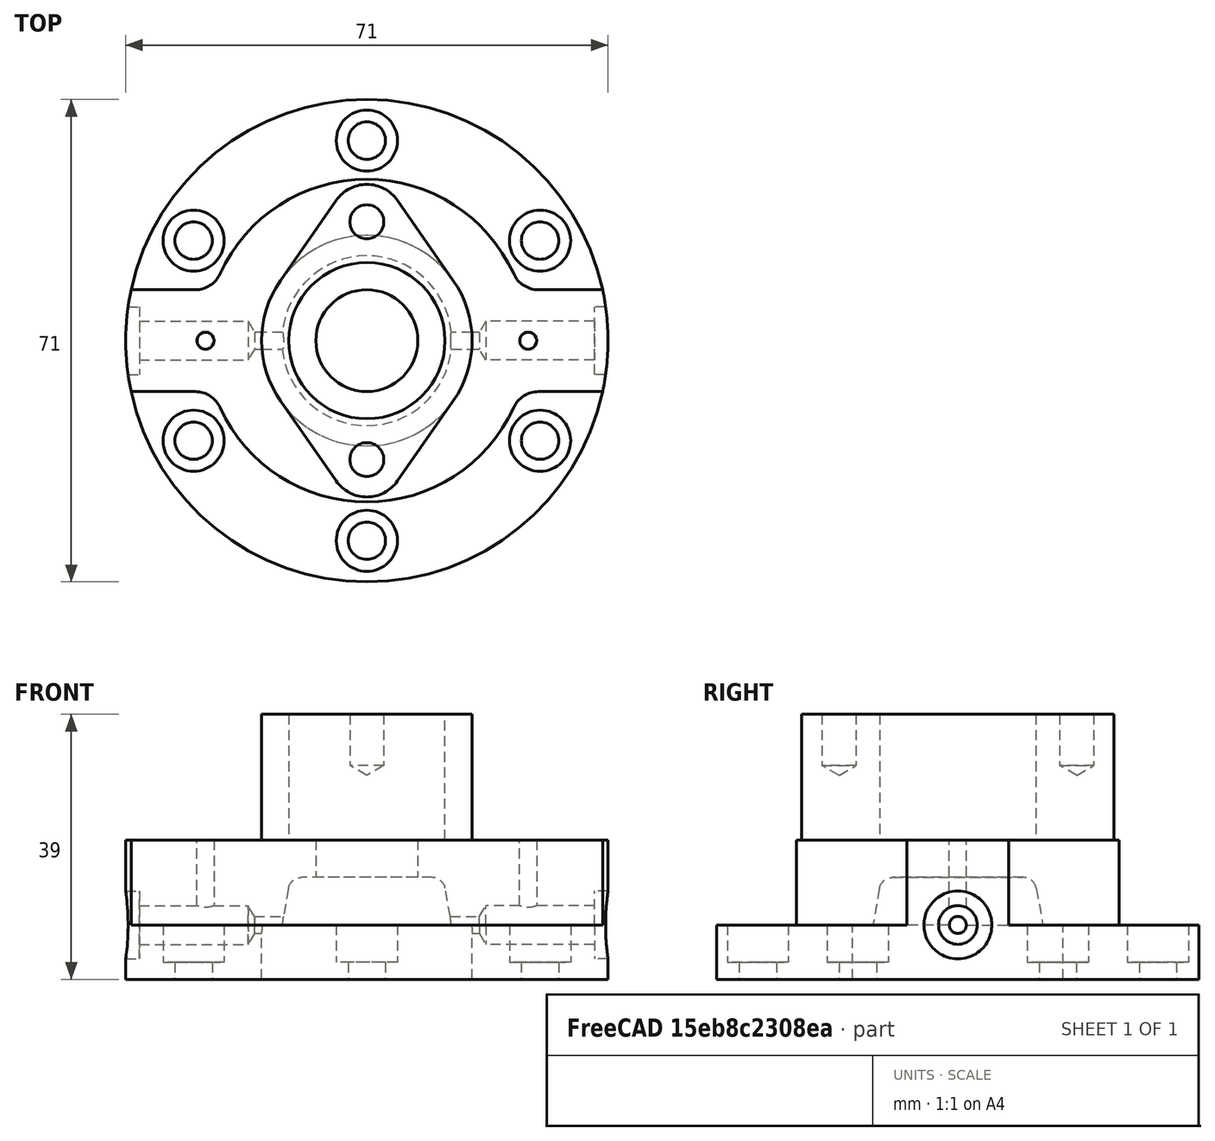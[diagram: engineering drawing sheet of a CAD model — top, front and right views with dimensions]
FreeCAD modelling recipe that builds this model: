
FCSTD DOCUMENT  (FreeCAD 1.1R40265 (Git))
Label: 0000
License: All rights reserved
LicenseURL: http://en.wikipedia.org/wiki/All_rights_reserved
objects: TechDraw::DrawViewDimension×33, Sketcher::SketchObject×10, PartDesign::Fillet×4, PartDesign::Pocket×3, PartDesign::Hole×3, TechDraw::DrawProjGroupItem×3, PartDesign::Mirrored×2, TechDraw::DrawViewSection×2, App::Point×1, PartDesign::Revolution×1, PartDesign::Pad×1, PartDesign::PolarPattern×1, Spreadsheet::Sheet×1, TechDraw::DrawSVGTemplate×1, PartDesign::Body×1, TechDraw::DrawViewAnnotation×1, TechDraw::DrawPage×1
note: 120 computed .brp shape members not serialized (recipe doc carries the construction recipe); baked Part::Feature solids carry a one-line shape summary decoded from their .brp

FEATURE [App::Point] Origin001
  Role = Origin
FEATURE [Sketcher::SketchObject] Sketch
  ArcFitTolerance = 1e-06
  AttachmentSupport = -> [XZ_Plane]
  ExternalTypes = [0]
  FullyConstrained = true
  MakeInternals = false
  MapMode = 5
  Placement = pos=(0,0,0) rot=(1,0,0;1.5708rad)
  expr: Constraints[0] = ModelParameters.Constraint_0_Distance
  expr: Constraints[12] = ModelParameters.Constraint_12_Distance
  expr: Constraints[15] = ModelParameters.Constraint_15_Distance
  expr: Constraints[18] = ModelParameters.Constraint_18_Distance
  expr: Constraints[22] = ModelParameters.Constraint_22_Angle
  expr: Constraints[25] = ModelParameters.Constraint_25_Radius
  expr: Constraints[3] = ModelParameters.Constraint_3_Distance
  expr: Constraints[6] = ModelParameters.Constraint_6_Distance
  expr: Constraints[9] = ModelParameters.Constraint_9_Distance
  sketch-geometry (10):
    g0: LineSegment [constr] StartX=0 StartY=0 StartZ=0 EndX=15.5 EndY=0 EndZ=0
    g1: LineSegment StartX=15.5 StartY=0 StartZ=0 EndX=35.5 EndY=0 EndZ=0
    g2: LineSegment StartX=35.5 StartY=0 StartZ=0 EndX=35.5 EndY=20.5 EndZ=0
    g3: LineSegment StartX=35.5 StartY=20.5 StartZ=0 EndX=7.5 EndY=20.5 EndZ=0
    g4: LineSegment StartX=7.5 StartY=20.5 StartZ=0 EndX=7.5 EndY=15 EndZ=0
    g5: LineSegment StartX=15.5 StartY=0 StartZ=0 EndX=15.5 EndY=8 EndZ=0
    g6: LineSegment StartX=15.5 StartY=8 StartZ=0 EndX=12.5 EndY=8 EndZ=0
    g7: LineSegment StartX=12.5 StartY=8 StartZ=0 EndX=11.5571 EndY=13.3473 EndZ=0
    g8: LineSegment StartX=7.5 StartY=15 StartZ=0 EndX=9.58751 EndY=15 EndZ=0
    g9: ArcOfCircle CenterX=9.58751 CenterY=13 CenterZ=0 NormalX=0 NormalY=0 NormalZ=1 AngleXU=0 Radius=2 StartAngle=0.174533 EndAngle=1.5708
  constraints (28):
    c: Distance(g0) = 15.5
    c: Coincident(g0,g-1)
    c: PointOnObject(g0,g-1)
    c: Distance(g1) = 20
    c: Coincident(g1,g0)
    c: PointOnObject(g1,g-1)
    c: Distance(g2) = 20.5
    c: Coincident(g2,g1)
    c: Vertical(g2)
    c: Distance(g3) = 28
    c: Coincident(g3,g2)
    c: Horizontal(g3)
    c: Distance(g4) = 5.5
    c: Coincident(g4,g3)
    c: Vertical(g4)
    c: Distance(g5) = 8
    c: Coincident(g5,g0)
    c: Vertical(g5)
    c: Distance(g6) = 3
    c: Coincident(g6,g5)
    c: Horizontal(g6)
    c: Coincident(g7,g6)
    c: Angle(g-2,g7) = 0.174533
    c: Coincident(g8,g4)
    c: Horizontal(g8)
    c: Radius(g9) = 2
    c: Tangent(g9,g7) = -1.5708
    c: Tangent(g9,g8) = 1.5708
FEATURE [PartDesign::Revolution] Revolution
  Angle = 360
  Angle2 = 60
  Axis = (0,2e-16,1)
  Base = (0,0,0)
  Placement = pos=(0,0,0) rot=(1,0,0;1.5708rad)
  Profile = -> Sketch
  ReferenceAxis = -> Sketch [V_Axis]
  Reversed = true
  Suppressed = false
  Type = 0
  expr: Angle = ModelParameters.Angle
FEATURE [Sketcher::SketchObject] Sketch001
  ArcFitTolerance = 1e-06
  AttachmentOffset = pos=(0,0,20.5) rot=(0,0,1;0rad)
  AttachmentSupport = -> [XY_Plane]
  ExternalTypes = [0]
  FullyConstrained = true
  MakeInternals = false
  MapMode = 5
  Placement = pos=(0,0,20.5) rot=(0,0,1;0rad)
  expr: Constraints[10] = ModelParameters.Constraint_9_Distance_001
  expr: Constraints[11] = ModelParameters.Constraint_9_Distance_001
  expr: Constraints[15] = ModelParameters.Constraint_15_Diameter_001
  expr: Constraints[19] = ModelParameters.Constraint_15_Diameter_001 / 2
  expr: Constraints[1] = ModelParameters.Constraint_1_Diameter
  expr: Constraints[22] = ModelParameters.Constraint_15_Diameter_001 / 2
  expr: Constraints[25] = ModelParameters.Constraint_25_Diameter
  expr: Constraints[27] = ModelParameters.Constraint_25_Diameter
  expr: Constraints[29] = ModelParameters.Constraint_29_Diameter
  expr: Constraints[38] = ModelParameters.Constraint_38_Distance
  expr: Constraints[8] = ModelParameters.Constraint_9_Distance_001
  expr: Constraints[9] = ModelParameters.Constraint_9_Distance_001
  sketch-geometry (14):
    g0: ArcOfCircle CenterX=0 CenterY=0 CenterZ=0 NormalX=0 NormalY=0 NormalZ=1 AngleXU=0 Radius=23.75 StartAngle=0.321289 EndAngle=2.8203
    g1: Circle [constr] CenterX=0 CenterY=0 CenterZ=0 NormalX=0 NormalY=0 NormalZ=1 AngleXU=0 Radius=35.5
    g2: LineSegment StartX=22.5347 StartY=-7.5 StartZ=0 EndX=34.6987 EndY=-7.5 EndZ=0
    g3: LineSegment StartX=-22.5347 StartY=7.5 StartZ=0 EndX=-34.6987 EndY=7.5 EndZ=0
    g4: LineSegment StartX=-22.5347 StartY=-7.5 StartZ=0 EndX=-34.6987 EndY=-7.5 EndZ=0
    g5: LineSegment StartX=22.5347 StartY=7.5 StartZ=0 EndX=34.6987 EndY=7.5 EndZ=0
    g6: ArcOfCircle CenterX=0 CenterY=0 CenterZ=0 NormalX=0 NormalY=0 NormalZ=1 AngleXU=0 Radius=23.75 StartAngle=3.46288 EndAngle=5.9619
    g7: LineSegment [constr] StartX=0 StartY=0 StartZ=0 EndX=23.75 EndY=0 EndZ=0
    g8: LineSegment [constr] StartX=0 StartY=0 StartZ=0 EndX=-23.75 EndY=0 EndZ=0
    g9: Circle CenterX=-23.75 CenterY=0 CenterZ=0 NormalX=0 NormalY=0 NormalZ=1 AngleXU=0 Radius=1.25
    g10: Circle CenterX=23.75 CenterY=0 CenterZ=0 NormalX=0 NormalY=0 NormalZ=1 AngleXU=0 Radius=1.25
    g11: Circle CenterX=0 CenterY=0 CenterZ=0 NormalX=0 NormalY=0 NormalZ=1 AngleXU=0 Radius=7.5
    g12: ArcOfCircle CenterX=0 CenterY=0 CenterZ=0 NormalX=0 NormalY=0 NormalZ=1 AngleXU=0 Radius=35.5 StartAngle=0.212872 EndAngle=2.92872
    g13: ArcOfCircle CenterX=-1.16293e-06 CenterY=0 CenterZ=0 NormalX=0 NormalY=0 NormalZ=1 AngleXU=0 Radius=35.5 StartAngle=3.35446 EndAngle=6.07031
  constraints (40):
    c: Coincident(g0,g-1)
    c: Diameter(g1) = 71
    c: Coincident(g1,g0)
    c: Horizontal(g2)
    c: PointOnObject(g3,g1)
    c: Horizontal(g3)
    c: Horizontal(g4)
    c: Horizontal(g5)
    c: Distance(g-1,g3) = 7.5
    c: Distance(g-1,g4) = 7.5
    c: Distance(g-1,g5) = 7.5
    c: Distance(g-1,g2) = 7.5
    c: Coincident(g2,g6)
    c: Coincident(g5,g0)
    c: Equal(g0,g6)
    c: Diameter(g0) = 47.5
    c: Coincident(g3,g0)
    c: Coincident(g4,g6)
    c: Coincident(g0,g6)
    c: Distance(g7) = 23.75
    c: Coincident(g7,g0)
    c: PointOnObject(g7,g-1)
    c: Distance(g8) = 23.75
    c: Coincident(g8,g0)
    c: PointOnObject(g8,g-1)
    c: Diameter(g9) = 2.5
    c: Coincident(g9,g8)
    c: Diameter(g10) = 2.5
    c: Coincident(g10,g7)
    c: Diameter(g11) = 15
    c: Coincident(g11,g0)
    c: Coincident(g12,g0)
    c: Coincident(g12,g3)
    c: Coincident(g12,g5)
    c: Coincident(g2,g13)
    c: Coincident(g4,g13)
    c: Block(g4)
    c: Block(g2)
    c: Distance(g4,g4) = 12.164
    c: Block(g13)
FEATURE [PartDesign::Pocket] Pocket
  BaseFeature = -> Revolution
  Direction = (0,0,-1)
  Length = 12.5
  Length2 = 5
  Placement = pos=(0,0,0) rot=(1,0,0;1.5708rad)
  Profile = -> Sketch001
  ReferenceAxis = -> Sketch001 [N_Axis]
  Suppressed = false
  Type = 0
  expr: Length = ModelParameters.Pocket_Length
  expr: TaperAngle = ModelParameters.Pocket_Taper_angle
FEATURE [Sketcher::SketchObject] Sketch002
  ArcFitTolerance = 1e-06
  AttachmentOffset = pos=(0,0,20.5) rot=(0,0,1;0rad)
  AttachmentSupport = -> [XY_Plane]
  ExternalTypes = [0]
  FullyConstrained = true
  MakeInternals = false
  MapMode = 5
  Placement = pos=(0,0,20.5) rot=(0,0,1;0rad)
  expr: Constraints[0] = ModelParameters.Constraint_0_Diameter
  expr: Constraints[22] = ModelParameters.Constraint_22_Radius
  expr: Constraints[4] = ModelParameters.Constraint_4_DistanceY
  expr: Constraints[5] = ModelParameters.Constraint_5_Radius
  sketch-geometry (12):
    g0: Circle CenterX=0 CenterY=0 CenterZ=0 NormalX=0 NormalY=0 NormalZ=1 AngleXU=0 Radius=11.5
    g1: Circle [constr] CenterX=0 CenterY=0 CenterZ=0 NormalX=0 NormalY=0 NormalZ=1 AngleXU=0 Radius=15.5
    g2: Circle [constr] CenterX=0 CenterY=17.5 CenterZ=0 NormalX=0 NormalY=0 NormalZ=1 AngleXU=0 Radius=5.5
    g3: Circle [constr] CenterX=0 CenterY=-17.5 CenterZ=0 NormalX=0 NormalY=0 NormalZ=1 AngleXU=0 Radius=5.5
    g4: LineSegment StartX=-4.51358 StartY=20.6429 StartZ=0 EndX=-12.7201 EndY=8.85714 EndZ=0
    g5: LineSegment StartX=4.51358 StartY=20.6429 StartZ=0 EndX=12.7201 EndY=8.85714 EndZ=0
    g6: LineSegment StartX=12.7201 StartY=-8.85714 StartZ=0 EndX=4.51359 EndY=-20.6429 EndZ=0
    g7: LineSegment StartX=-12.7201 StartY=-8.85714 StartZ=0 EndX=-4.51358 EndY=-20.6429 EndZ=0
    g8: ArcOfCircle CenterX=3.6e-15 CenterY=7e-16 CenterZ=0 NormalX=0 NormalY=0 NormalZ=1 AngleXU=0 Radius=15.5 StartAngle=2.53335 EndAngle=3.74984
    g9: ArcOfCircle CenterX=3.6e-15 CenterY=7e-16 CenterZ=0 NormalX=0 NormalY=0 NormalZ=1 AngleXU=0 Radius=15.5 StartAngle=5.67494 EndAngle=6.89143
    g10: ArcOfCircle CenterX=0 CenterY=17.5 CenterZ=0 NormalX=0 NormalY=0 NormalZ=1 AngleXU=0 Radius=5.5 StartAngle=0.608246 EndAngle=2.53335
    g11: ArcOfCircle CenterX=0 CenterY=-17.5 CenterZ=0 NormalX=0 NormalY=0 NormalZ=1 AngleXU=0 Radius=5.5 StartAngle=3.74984 EndAngle=5.67494
  constraints (26):
    c: Diameter(g0) = 23
    c: Coincident(g0,g-1)
    c: Coincident(g1,g0)
    c: PointOnObject(g3,g-2)
    c: DistanceY(g3,g0) = 17.5
    c: Radius(g3) = 5.5
    c: Tangent(g5,g2) = 1.5708
    c: Tangent(g5,g1) = 1.5708
    c: Tangent(g6,g1) = 1.5708
    c: Tangent(g7,g3) = -1.5708
    c: Coincident(g9,g8)
    c: Coincident(g9,g5)
    c: Coincident(g9,g6)
    c: Coincident(g4,g8)
    c: Coincident(g7,g8)
    c: Coincident(g10,g2)
    c: Coincident(g10,g4)
    c: Coincident(g11,g3)
    c: Coincident(g11,g7)
    c: Block(g5)
    c: Block(g4)
    c: Coincident(g6,g11)
    c: Radius(g9) = 15.5
    c: Coincident(g5,g10)
    c: Block(g6)
    c: Block(g7)
FEATURE [PartDesign::Fillet] Fillet
  Base = -> Pocket [Edge25]
  BaseFeature = -> Pocket
  Placement = pos=(0,0,0) rot=(1,0,0;1.5708rad)
  Radius = 4
  SupportTransform = false
  Suppressed = false
  UseAllEdges = false
  expr: Radius = ModelParameters.Radius
FEATURE [PartDesign::Fillet] Fillet001
  Base = -> Fillet [Edge15]
  BaseFeature = -> Fillet
  Placement = pos=(0,0,0) rot=(1,0,0;1.5708rad)
  Radius = 4
  SupportTransform = false
  Suppressed = false
  UseAllEdges = false
  expr: Radius = ModelParameters.Radius
FEATURE [PartDesign::Fillet] Fillet002
  Base = -> Fillet001 [Edge32]
  BaseFeature = -> Fillet001
  Placement = pos=(0,0,0) rot=(1,0,0;1.5708rad)
  Radius = 4
  SupportTransform = false
  Suppressed = false
  UseAllEdges = false
  expr: Radius = ModelParameters.Radius
FEATURE [PartDesign::Fillet] Fillet003
  Base = -> Fillet002 [Edge28]
  BaseFeature = -> Fillet002
  Placement = pos=(0,0,0) rot=(1,0,0;1.5708rad)
  Radius = 4
  SupportTransform = false
  Suppressed = false
  UseAllEdges = false
  expr: Radius = ModelParameters.Radius
FEATURE [PartDesign::Pad] Pad
  BaseFeature = -> Fillet003
  Direction = (0,0,1)
  Length = 18.5
  Length2 = 10
  Placement = pos=(0,0,0) rot=(1,0,0;1.5708rad)
  Profile = -> Sketch002
  ReferenceAxis = -> Sketch002 [N_Axis]
  Suppressed = false
  Type = 0
  expr: Length = ModelParameters.Length
FEATURE [Sketcher::SketchObject] Sketch003
  ArcFitTolerance = 1e-06
  AttachmentOffset = pos=(0,0,39) rot=(0,0,1;0rad)
  AttachmentSupport = -> [XY_Plane]
  ExternalTypes = [0]
  FullyConstrained = true
  MakeInternals = false
  MapMode = 5
  Placement = pos=(0,0,39) rot=(0,0,1;0rad)
  expr: Constraints[0] = ModelParameters.Constraint_0_Diameter_003
  expr: Constraints[2] = ModelParameters.Constraint_0_Diameter_003
  expr: Constraints[4] = ModelParameters.Constraint_4_DistanceY_003
  sketch-geometry (2):
    g0: Circle CenterX=0 CenterY=17.5 CenterZ=0 NormalX=0 NormalY=0 NormalZ=1 AngleXU=0 Radius=2.5
    g1: Circle CenterX=0 CenterY=-17.5 CenterZ=0 NormalX=0 NormalY=0 NormalZ=1 AngleXU=0 Radius=2.5
  constraints (5):
    c: Diameter(g0) = 5
    c: PointOnObject(g0,g-2)
    c: Diameter(g1) = 5
    c: Symmetric(g0,g1,g-1)
    c: DistanceY(g-1,g0) = 17.5
FEATURE [PartDesign::Hole] Hole
  BaseFeature = -> Pad
  CustomThreadClearance = 0
  Depth = 7.5
  DepthType = 0
  Diameter = 5
  DrillForDepth = false
  DrillPoint = 1
  DrillPointAngle = 118
  HoleCutCountersinkAngle = 90
  HoleCutCustomValues = false
  HoleCutDepth = 0
  HoleCutDiameter = 0
  HoleCutType = 0
  ModelThread = false
  Placement = pos=(0,0,0) rot=(1,0,0;1.5708rad)
  Profile = -> Sketch003
  Suppressed = false
  Tapered = false
  TaperedAngle = 90
  ThreadClass = 0
  ThreadDepth = 7.5
  ThreadDepthType = 0
  ThreadDiameter = 5
  ThreadDirection = 0
  ThreadFit = 0
  ThreadSize = 0
  ThreadType = 0
  Threaded = false
  UseCustomThreadClearance = false
  expr: Depth = ModelParameters.Depth
  expr: Diameter = ModelParameters.Diameter
  expr: DrillPointAngle = ModelParameters.Drill_Angle
FEATURE [Sketcher::SketchObject] Sketch004
  ArcFitTolerance = 1e-06
  AttachmentOffset = pos=(0,0,8) rot=(0,0,1;0rad)
  AttachmentSupport = -> [XY_Plane]
  ExternalTypes = [0]
  FullyConstrained = true
  MakeInternals = false
  MapMode = 5
  Placement = pos=(0,0,8) rot=(0,0,1;0rad)
  expr: Constraints[0] = ModelParameters.Constraint_0_Diameter_004
  expr: Constraints[2] = ModelParameters.Constraint_2_DistanceY_004
  sketch-geometry (1):
    g0: Circle CenterX=0 CenterY=29.45 CenterZ=0 NormalX=0 NormalY=0 NormalZ=1 AngleXU=0 Radius=2.75
  constraints (3):
    c: Diameter(g0) = 5.5
    c: PointOnObject(g0,g-2)
    c: DistanceY(g-1,g0) = 29.45
FEATURE [PartDesign::Hole] Hole001
  BaseFeature = -> Hole
  CustomThreadClearance = 0
  Depth = 216.866
  DepthType = 1
  Diameter = 5.5
  DrillForDepth = false
  DrillPoint = 1
  DrillPointAngle = 118
  HoleCutCountersinkAngle = 90
  HoleCutCustomValues = false
  HoleCutDepth = 5.5
  HoleCutDiameter = 9
  HoleCutType = 1
  ModelThread = false
  Placement = pos=(0,0,0) rot=(1,0,0;1.5708rad)
  Profile = -> Sketch004
  Suppressed = false
  Tapered = false
  TaperedAngle = 90
  ThreadClass = 0
  ThreadDepth = 216.866
  ThreadDepthType = 0
  ThreadDiameter = 5.5
  ThreadDirection = 0
  ThreadFit = 0
  ThreadSize = 0
  ThreadType = 0
  Threaded = false
  UseCustomThreadClearance = false
  expr: Diameter = ModelParameters.Diameter_001
  expr: HoleCutDepth = ModelParameters.Head_Depth
  expr: HoleCutDiameter = ModelParameters.Head_Diameter
FEATURE [PartDesign::PolarPattern] PolarPattern
  Angle = 60
  Axis = -> Sketch004 [N_Axis]
  BaseFeature = -> Hole001
  Mode = 1
  Occurrences = 6
  Offset = 60
  Originals = -> [Hole001]
  Placement = pos=(0,0,0) rot=(1,0,0;1.5708rad)
  Suppressed = false
  TransformMode = 0
FEATURE [Sketcher::SketchObject] Sketch005
  ArcFitTolerance = 1e-06
  AttachmentOffset = pos=(0,0,35.5) rot=(0,0,1;0rad)
  AttachmentSupport = -> [YZ_Plane]
  ExternalTypes = [0]
  FullyConstrained = true
  MakeInternals = false
  MapMode = 5
  Placement = pos=(35.5,0,0) rot=(0.57735,0.57735,0.57735;2.0944rad)
  expr: Constraints[0] = ModelParameters.Constraint_0_Diameter_005
  expr: Constraints[2] = ModelParameters.Constraint_2_DistanceY_005
  sketch-geometry (1):
    g0: Circle CenterX=0 CenterY=8 CenterZ=0 NormalX=0 NormalY=0 NormalZ=1 AngleXU=0 Radius=2.85
  constraints (3):
    c: Diameter(g0) = 5.7
    c: PointOnObject(g0,g-2)
    c: DistanceY(g-1,g0) = 8
FEATURE [PartDesign::Hole] Hole002
  BaseFeature = -> PolarPattern
  CustomThreadClearance = 0
  Depth = 18
  DepthType = 0
  Diameter = 5.7
  DrillForDepth = false
  DrillPoint = 1
  DrillPointAngle = 118
  HoleCutCountersinkAngle = 90
  HoleCutCustomValues = false
  HoleCutDepth = 2
  HoleCutDiameter = 10
  HoleCutType = 1
  ModelThread = false
  Placement = pos=(0,0,0) rot=(1,0,0;1.5708rad)
  Profile = -> Sketch005
  Suppressed = false
  Tapered = false
  TaperedAngle = 90
  ThreadClass = 0
  ThreadDepth = 18
  ThreadDepthType = 0
  ThreadDiameter = 5.7
  ThreadDirection = 0
  ThreadFit = 0
  ThreadSize = 0
  ThreadType = 0
  Threaded = false
  UseCustomThreadClearance = false
  expr: Depth = ModelParameters.Depth_002
  expr: Diameter = ModelParameters.Diameter_002
  expr: DrillPointAngle = ModelParameters.Drill_Angle002
  expr: HoleCutDepth = ModelParameters.Head_Depth002
  expr: HoleCutDiameter = ModelParameters.Head_Diameter002
FEATURE [PartDesign::Mirrored] Mirrored
  BaseFeature = -> Hole002
  MirrorPlane = -> YZ_Plane
  Originals = -> [Hole002]
  Placement = pos=(0,0,0) rot=(1,0,0;1.5708rad)
  Suppressed = false
  TransformMode = 0
FEATURE [Sketcher::SketchObject] Sketch006
  ArcFitTolerance = 1e-06
  AttachmentOffset = pos=(0,0,35.5) rot=(0,0,1;0rad)
  AttachmentSupport = -> [YZ_Plane]
  ExternalTypes = [0]
  FullyConstrained = true
  MakeInternals = false
  MapMode = 5
  Placement = pos=(35.5,0,0) rot=(0.57735,0.57735,0.57735;2.0944rad)
  expr: Constraints[0] = ModelParameters.Constraint_0_Diameter006
  expr: Constraints[2] = ModelParameters.Constraint_2_DistanceY_006
  sketch-geometry (1):
    g0: Circle CenterX=0 CenterY=8 CenterZ=0 NormalX=0 NormalY=0 NormalZ=1 AngleXU=0 Radius=1
  constraints (3):
    c: Diameter(g0) = 2
    c: PointOnObject(g0,g-2)
    c: DistanceY(g-1,g0) = 8
FEATURE [PartDesign::Pocket] Pocket001
  BaseFeature = -> Mirrored
  Direction = (-1,0,0)
  Length = 5
  Length2 = 5
  Placement = pos=(0,0,0) rot=(1,0,0;1.5708rad)
  Profile = -> Sketch006
  ReferenceAxis = -> Sketch006 [N_Axis]
  Suppressed = false
  Type = 0
  expr: Length = ModelParameters.Pocket_Length001
  expr: TaperAngle = ModelParameters.Taper_Angle
FEATURE [Spreadsheet::Sheet] ModelParameters
  cells = A1='OBJECT; B1='PARAMETER; C1='VALUE; A2='Sketch; B2='Constraint_0_Distance; C2(Constraint_0_Distance)=15.5; A3='Sketch; B3='Constraint_3_Distance; C3(Constraint_3_Distance)=20; A4='Sketch; B4='Constraint_6_Distance; C4(Constraint_6_Distance)=20.5; A5='Sketch; B5='Constraint_9_Distance; C5(Constraint_9_Distance)=28; A6='Sketch; B6='Constraint_12_Distance; C6(Constraint_12_Distance)=5.5; A7='Sketch; B7='Constraint_15_Distance; C7(Constraint_15_Distance)=8; A8='Sketch; B8='Constraint_18_Distance; C8(Constraint_18_Distance)=3; A9='Sketch; B9='Constraint_22_Angle; C9(Constraint_22_Angle)=10; A10='Sketch; B10='Constraint_25_Radius; C10(Constraint_25_Radius)=2; A11='Revolution; B11='Angle; C11(Angle)==360 deg; A12='Sketch001; B12='Constraint_1_Diameter; C12(Constraint_1_Diameter)=71; A13='Sketch001; B13='Constraint_9_Distance; C13(Constraint_9_Distance_001)=7.5; A14='Sketch001; B14='Constraint_15_Diameter; C14(Constraint_15_Diameter_001)=47.5; A15='Sketch001; B15='Constraint_25_Diameter; C15(Constraint_25_Diameter)=2.5; A16='Sketch001; B16='Constraint_29_Diameter; C16(Constraint_29_Diameter)=15; A17='Sketch001; B17='Constraint_38_Distance; C17(Constraint_38_Distance)=12.16401; A18='Pocket; B18='Length; C18(Pocket_Length)==12.5 mm; A19='Pocket; B19='Taper Angle; C19(Pocket_Taper_angle)=0; A20='Sketch002; B20='Constraint_0_Diameter; C20(Constraint_0_Diameter)=23; A21='Sketch002; B21='Constraint_4_DistanceY; C21(Constraint_4_DistanceY)=17.5; A22='Sketch002; B22='Constraint_5_Radius; C22(Constraint_5_Radius)=5.5; A23='Sketch002; B23='Constraint_22_Radius; C23(Constraint_22_Radius)=15.5; A24='Fillet; B24='Radius; C24(Radius)==4 mm; A25='Pad; B25='Length; C25(Length)=18.5; A26='Sketch003; B26='Constraint_0_Diameter; C26(Constraint_0_Diameter_003)=5; A27='Sketch003; B27='Constraint_4_DistanceY; C27(Constraint_4_DistanceY_003)=17.5; A28='Hole; B28='Diameter; C28(Diameter)==5 mm; A29='Hole; B29='Depth; C29(Depth)==7.5 mm; A30='Hole; B30='Drill Angle; C30(Drill_Angle)=118; A31='Sketch004; B31='Constraint_0_Diameter; C31(Constraint_0_Diameter_004)=5.5; A32='Sketch004; B32='Constraint_2_DistanceY; C32(Constraint_2_DistanceY_004)=29.45; A33='Hole001; B33='Diameter; C33(Diameter_001)==5.5 mm; A34='Hole001; B34='Head Diameter; C34(Head_Diameter)=9; A35='Hole001; B35='Head Depth; C35(Head_Depth)=5.5; A36='Sketch005; B36='Constraint_0_Diameter; C36(Constraint_0_Diameter_005)=5.7; A37='Sketch005; B37='Constraint_2_DistanceY; C37(Constraint_2_DistanceY_005)=8; A38='Hole002; B38='Diameter; C38(Diameter_002)==5.7 mm; A39='Hole002; B39='Depth; C39(Depth_002)==18 mm; A40='Hole002; B40='Head Diameter; C40(Head_Diameter002)=10; A41='Hole002; B41='Head Depth; C41(Head_Depth002)=2; A42='Hole002; B42='Drill Angle; C42(Drill_Angle002)=118; A43='Sketch006; B43='Constraint_0_Diameter; C43(Constraint_0_Diameter006)=2; A44='Sketch006; B44='Constraint_2_DistanceY; C44(Constraint_2_DistanceY_006)=8; A45='Pocket001; B45='Length; C45(Pocket_Length001)==5 mm; A46='Pocket001; B46='Taper Angle; C46(Taper_Angle)=0; A47='Sketch009; B47='Diameter; C47(Diameter009)=2.5; A48='Sketch009; B48='Height From Base; C48(Height_from_base)=8
FEATURE [PartDesign::Mirrored] Mirrored001
  BaseFeature = -> Pocket001
  MirrorPlane = -> Sketch005 [V_Axis]
  Originals = -> [Hole002]
  Placement = pos=(0,0,0) rot=(1,0,0;1.5708rad)
  Suppressed = false
  TransformMode = 0
FEATURE [TechDraw::DrawSVGTemplate] Template
  EditableTexts = Designed_by_Name=UGWOKE, K.P.; Drawing_number=977; FC-Date=06-08-2025; FC-SC=1:1; FC-SH=1/1; FC-Title=SPREADSHEET PRACTICE; Subtitle=TECHDRAW PART; Weight=Weight
  Height = 210
  Orientation = 1
  Template = C:/Program Files/FreeCAD_0.19.24267-Win-Conda_vc14.x-x86_64/data/Mod/TechDraw/Templates/A4_LandscapeTD.svg
  Width = 297
FEATURE [Sketcher::SketchObject] Sketch007
  ArcFitTolerance = 1e-06
  ExternalTypes = [0]
  FullyConstrained = true
  MakeInternals = false
  Placement = pos=(0,0,38) rot=(0,0,1;0rad)
  sketch-geometry (1):
    g0: LineSegment [constr] StartX=-40.41 StartY=0 StartZ=0 EndX=45.33 EndY=0 EndZ=0
  constraints (4):
    c: PointOnObject(g0,g-1)
    c: PointOnObject(g0,g-1)
    c: DistanceX(g0,g-1) = 40.41
    c: DistanceX(g-1,g0) = 45.33
FEATURE [Sketcher::SketchObject] Sketch008
  ArcFitTolerance = 1e-06
  ExternalTypes = [0]
  FullyConstrained = true
  MakeInternals = false
  Placement = pos=(0,0,38) rot=(0,0,1;0rad)
  sketch-geometry (1):
    g0: LineSegment [constr] StartX=0 StartY=42.94 StartZ=0 EndX=0 EndY=-43.59 EndZ=0
  constraints (4):
    c: PointOnObject(g0,g-2)
    c: PointOnObject(g0,g-2)
    c: DistanceY(g-1,g0) = 42.94
    c: DistanceY(g0,g-1) = 43.59
FEATURE [Sketcher::SketchObject] Sketch009
  ArcFitTolerance = 1e-06
  ExternalTypes = [0]
  FullyConstrained = true
  MakeInternals = false
  Placement = pos=(35.5,0,0) rot=(0.57735,0.57735,0.57735;2.0944rad)
  expr: Constraints[0] = ModelParameters.Diameter009
  expr: Constraints[2] = ModelParameters.Height_from_base
  sketch-geometry (1):
    g0: Circle CenterX=0 CenterY=8 CenterZ=0 NormalX=0 NormalY=0 NormalZ=1 AngleXU=0 Radius=1.25
  constraints (3):
    c: Diameter(g0) = 2.5
    c: PointOnObject(g0,g-2)
    c: DistanceY(g-1,g0) = 8
FEATURE [PartDesign::Pocket] Pocket002
  BaseFeature = -> Mirrored001
  Direction = (-1,1e-16,-2e-16)
  Length = 5
  Length2 = 5
  Placement = pos=(0,0,0) rot=(1,0,0;1.5708rad)
  Profile = -> Sketch009 [Edge1]
  ReferenceAxis = -> Sketch009 [N_Axis]
  Suppressed = false
  Type = 1
FEATURE [PartDesign::Body] Body
  AllowCompound = false
  Group = -> [Sketch,Revolution,Sketch001,Pocket,Sketch002,Fillet,Fillet001,Fillet002,Fillet003,Pad,Sketch003,Hole,Sketch004,Hole001,PolarPattern,Sketch005,Hole002,Mirrored,Sketch006,Pocket001,Mirrored001,Sketch009,Pocket002]
  Origin = -> Origin
  Tip = -> Pocket002
FEATURE [TechDraw::DrawProjGroupItem] View
  CoarseView = false
  Direction = (0,0,1)
  Focus = 100
  HardHidden = false
  IsoCount = 0
  IsoHidden = false
  IsoVisible = false
  LockPosition = false
  Perspective = false
  Rotation = 0
  RotationVector = (1,0,0)
  ScaleType = 0
  ScrubCount = 1
  SeamHidden = false
  SeamVisible = false
  SmoothHidden = false
  SmoothVisible = true
  Source = -> [Body]
  Type = 0
  X = 70.2364
  XDirection = (1,0,0)
  Y = 161.598
FEATURE [TechDraw::DrawViewSection] SectionView  label="Section  - "
  BaseView = -> View
  CoarseView = false
  CutSurfaceDisplay = 2
  Direction = (1e-16,-1,0)
  FileGeomPattern = C:/Program Files/FreeCAD_0.19.24267-Win-Conda_vc14.x-x86_64/data/Mod/TechDraw/PAT/FCPAT.pat
  FileHatchPattern = C:/Program Files/FreeCAD_0.19.24267-Win-Conda_vc14.x-x86_64/data/Mod/TechDraw/Patterns/simple.svg
  Focus = 100
  FuseBeforeCut = false
  HardHidden = false
  HatchOffset = (0,0,0)
  HatchRotation = 0
  HatchScale = 1
  IsoCount = 0
  IsoHidden = false
  IsoVisible = false
  LockPosition = false
  NameGeomPattern = Diamond
  Perspective = false
  Rotation = 0
  ScaleType = 2
  ScrubCount = 1
  SeamHidden = false
  SeamVisible = false
  SectionDirection = 4
  SectionLineStretch = 1
  SectionNormal = (1e-16,-1,0)
  SectionOrigin = (-2,0,19)
  SmoothHidden = false
  SmoothVisible = true
  Source = -> [Body]
  TrimAfterCut = false
  UsePreviousCut = false
  X = 70.0718
  XDirection = (1,1e-16,0)
  Y = 65.7859
FEATURE [TechDraw::DrawProjGroupItem] View001
  CoarseView = false
  Direction = (0,0,1)
  Focus = 100
  HardHidden = false
  IsoCount = 0
  IsoHidden = false
  IsoVisible = false
  LockPosition = false
  Perspective = false
  Rotation = 0
  RotationVector = (1,0,0)
  ScaleType = 0
  ScrubCount = 1
  SeamHidden = false
  SeamVisible = false
  SmoothHidden = false
  SmoothVisible = true
  Source = -> [Body]
  Type = 0
  X = -1128.45
  XDirection = (1e-16,1,0)
  Y = 974.428
FEATURE [TechDraw::DrawViewSection] SectionView001  label="Section001  - "
  BaseView = -> View001
  CoarseView = false
  CutSurfaceDisplay = 2
  Direction = (1,0,0)
  FileGeomPattern = C:/Program Files/FreeCAD_0.19.24267-Win-Conda_vc14.x-x86_64/data/Mod/TechDraw/PAT/FCPAT.pat
  FileHatchPattern = C:/Program Files/FreeCAD_0.19.24267-Win-Conda_vc14.x-x86_64/data/Mod/TechDraw/Patterns/simple.svg
  Focus = 100
  FuseBeforeCut = false
  HardHidden = false
  HatchOffset = (0,0,0)
  HatchRotation = 0
  HatchScale = 1
  IsoCount = 0
  IsoHidden = false
  IsoVisible = false
  LockPosition = false
  NameGeomPattern = Diamond
  Perspective = false
  Rotation = 0
  ScaleType = 0
  ScrubCount = 1
  SeamHidden = false
  SeamVisible = false
  SectionDirection = 4
  SectionLineStretch = 1
  SectionNormal = (1,0,0)
  SectionOrigin = (0,0,19)
  SmoothHidden = false
  SmoothVisible = true
  Source = -> [Body]
  TrimAfterCut = false
  UsePreviousCut = false
  X = 199.483
  XDirection = (0,1,0)
  Y = 89.27
FEATURE [TechDraw::DrawViewDimension] Dimension
  AngleOverride = false
  Arbitrary = false
  ArbitraryTolerances = false
  BoxCorners = (2) [(-35.5,-35.5,0),(35.5,35.5,0)]
  EqualTolerance = true
  ExtensionAngle = 0
  FormatSpec = R%.2w
  FormatSpecOverTolerance = %+.2w
  FormatSpecUnderTolerance = %+.2w
  Inverted = false
  LineAngle = 0
  LockPosition = false
  MeasureType = 1
  OverTolerance = 0
  References2D = -> [View]
  Rotation = 0
  ScaleType = 0
  ShowUnits = false
  TheoreticalExact = false
  Type = 4
  UnderTolerance = 0
  UseActualArea = true
  X = 29.4183
  Y = 33.602
FEATURE [TechDraw::DrawViewDimension] Dimension002
  AngleOverride = false
  Arbitrary = false
  ArbitraryTolerances = false
  BoxCorners = (2) [(-35.5,-35.5,0),(35.5,35.5,0)]
  EqualTolerance = true
  ExtensionAngle = 0
  FormatSpec = ⌀%.2w
  FormatSpecOverTolerance = %+.2w
  FormatSpecUnderTolerance = %+.2w
  Inverted = false
  LineAngle = 0
  LockPosition = false
  MeasureType = 1
  OverTolerance = 0
  References2D = -> [View]
  Rotation = 0
  ScaleType = 0
  ShowUnits = false
  TheoreticalExact = false
  Type = 5
  UnderTolerance = 0
  UseActualArea = true
  X = -32.0083
  Y = 30.7059
FEATURE [TechDraw::DrawViewDimension] Dimension003
  AngleOverride = false
  Arbitrary = false
  ArbitraryTolerances = false
  BoxCorners = (2) [(-35.5,-35.5,0),(35.5,35.5,0)]
  EqualTolerance = true
  ExtensionAngle = 0
  FormatSpec = ⌀%.2w
  FormatSpecOverTolerance = %+.2w
  FormatSpecUnderTolerance = %+.2w
  Inverted = false
  LineAngle = 0
  LockPosition = false
  MeasureType = 1
  OverTolerance = 0
  References2D = -> [View]
  Rotation = 0
  ScaleType = 0
  ShowUnits = false
  TheoreticalExact = false
  Type = 5
  UnderTolerance = 0
  UseActualArea = true
  X = 13.98
  Y = -42.5245
FEATURE [TechDraw::DrawViewDimension] Dimension004
  AngleOverride = false
  Arbitrary = false
  ArbitraryTolerances = false
  BoxCorners = (2) [(-35.5,-35.5,0),(35.5,35.5,0)]
  EqualTolerance = true
  ExtensionAngle = 0
  FormatSpec = %.2w
  FormatSpecOverTolerance = %+.2w
  FormatSpecUnderTolerance = %+.2w
  Inverted = false
  LineAngle = 0
  LockPosition = false
  MeasureType = 1
  OverTolerance = 0
  References2D = -> [View]
  Rotation = 0
  ScaleType = 0
  ShowUnits = false
  TheoreticalExact = false
  Type = 2
  UnderTolerance = 0
  UseActualArea = true
  X = -46.4624
  Y = 1e-06
FEATURE [TechDraw::DrawViewDimension] Dimension006
  AngleOverride = false
  Arbitrary = false
  ArbitraryTolerances = false
  BoxCorners = (2) [(-35.5,-35.5,0),(35.5,35.5,0)]
  EqualTolerance = true
  ExtensionAngle = 0
  FormatSpec = R%.2w
  FormatSpecOverTolerance = %+.2w
  FormatSpecUnderTolerance = %+.2w
  Inverted = false
  LineAngle = 0
  LockPosition = false
  MeasureType = 1
  OverTolerance = 0
  References2D = -> [View]
  Rotation = 0
  ScaleType = 0
  ShowUnits = false
  TheoreticalExact = false
  Type = 4
  UnderTolerance = 0
  UseActualArea = true
  X = 16.3531
  Y = 4.9393
FEATURE [TechDraw::DrawViewDimension] Dimension007
  AngleOverride = false
  Arbitrary = false
  ArbitraryTolerances = false
  BoxCorners = (2) [(-35.5,-19,-1e-07),(35.5,19,1e-07)]
  EqualTolerance = true
  ExtensionAngle = 0
  FormatSpec = %.2w
  FormatSpecOverTolerance = %+.2w
  FormatSpecUnderTolerance = %+.2w
  Inverted = false
  LineAngle = 0
  LockPosition = false
  MeasureType = 1
  OverTolerance = 0
  References2D = -> [SectionView]
  Rotation = 0
  ScaleType = 0
  ShowUnits = false
  TheoreticalExact = false
  Type = 0
  UnderTolerance = 0
  UseActualArea = true
  X = 0
  Y = 28.8176
FEATURE [TechDraw::DrawViewDimension] Dimension008
  AngleOverride = false
  Arbitrary = false
  ArbitraryTolerances = false
  BoxCorners = (2) [(-35.5,-19,-1e-07),(35.5,19,1e-07)]
  EqualTolerance = true
  ExtensionAngle = 0
  FormatSpec = %.2w
  FormatSpecOverTolerance = %+.2w
  FormatSpecUnderTolerance = %+.2w
  Inverted = false
  LineAngle = 0
  LockPosition = false
  MeasureType = 1
  OverTolerance = 0
  References2D = -> [SectionView]
  Rotation = 0
  ScaleType = 0
  ShowUnits = false
  TheoreticalExact = false
  Type = 0
  UnderTolerance = 0
  UseActualArea = true
  X = -34.6437
  Y = 10.5532
FEATURE [TechDraw::DrawViewDimension] Dimension009
  AngleOverride = false
  Arbitrary = false
  ArbitraryTolerances = false
  BoxCorners = (2) [(-35.5,-19,-1e-07),(35.5,19,1e-07)]
  EqualTolerance = true
  ExtensionAngle = 0
  FormatSpec = %.2w
  FormatSpecOverTolerance = %+.2w
  FormatSpecUnderTolerance = %+.2w
  Inverted = false
  LineAngle = 0
  LockPosition = false
  MeasureType = 1
  OverTolerance = 0
  References2D = -> [SectionView]
  Rotation = 0
  ScaleType = 0
  ShowUnits = false
  TheoreticalExact = false
  Type = 0
  UnderTolerance = 0
  UseActualArea = true
  X = -47.8511
  Y = 8.3002
FEATURE [TechDraw::DrawViewDimension] Dimension010
  AngleOverride = false
  Arbitrary = false
  ArbitraryTolerances = false
  BoxCorners = (2) [(-35.5,-19,-1e-07),(35.5,19,1e-07)]
  EqualTolerance = true
  ExtensionAngle = 0
  FormatSpec = %.2w
  FormatSpecOverTolerance = %+.2w
  FormatSpecUnderTolerance = %+.2w
  Inverted = false
  LineAngle = 0
  LockPosition = false
  MeasureType = 1
  OverTolerance = 0
  References2D = -> [SectionView]
  Rotation = 0
  ScaleType = 0
  ShowUnits = false
  TheoreticalExact = false
  Type = 0
  UnderTolerance = 0
  UseActualArea = true
  X = -54.8511
  Y = -11
FEATURE [TechDraw::DrawViewDimension] Dimension011
  AngleOverride = false
  Arbitrary = false
  ArbitraryTolerances = false
  BoxCorners = (2) [(-35.5,-19,-1e-07),(35.5,19,1e-07)]
  EqualTolerance = true
  ExtensionAngle = 0
  FormatSpec = %.2w
  FormatSpecOverTolerance = %+.2w
  FormatSpecUnderTolerance = %+.2w
  Inverted = false
  LineAngle = 0
  LockPosition = false
  MeasureType = 1
  OverTolerance = 0
  References2D = -> [SectionView]
  Rotation = 0
  ScaleType = 0
  ShowUnits = false
  TheoreticalExact = false
  Type = 0
  UnderTolerance = 0
  UseActualArea = true
  X = -40.266
  Y = -24.8734
FEATURE [TechDraw::DrawViewDimension] Dimension013
  AngleOverride = false
  Arbitrary = false
  ArbitraryTolerances = false
  BoxCorners = (2) [(-35.5,-19,-1e-07),(35.5,19,1e-07)]
  EqualTolerance = true
  ExtensionAngle = 0
  FormatSpec = %.2w
  FormatSpecOverTolerance = %+.2w
  FormatSpecUnderTolerance = %+.2w
  Inverted = false
  LineAngle = 0
  LockPosition = false
  MeasureType = 1
  OverTolerance = 0
  References2D = -> [SectionView]
  Rotation = 0
  ScaleType = 0
  ShowUnits = false
  TheoreticalExact = false
  Type = 0
  UnderTolerance = 0
  UseActualArea = true
  X = -3.14664
  Y = -37.9536
FEATURE [TechDraw::DrawViewDimension] Dimension014
  AngleOverride = false
  Arbitrary = false
  ArbitraryTolerances = false
  BoxCorners = (2) [(-35.5,-19,-1e-07),(35.5,19,1e-07)]
  EqualTolerance = true
  ExtensionAngle = 0
  FormatSpec = %.2w
  FormatSpecOverTolerance = %+.2w
  FormatSpecUnderTolerance = %+.2w
  Inverted = false
  LineAngle = 0
  LockPosition = false
  MeasureType = 1
  OverTolerance = 0
  References2D = -> [SectionView]
  Rotation = 0
  ScaleType = 0
  ShowUnits = false
  TheoreticalExact = false
  Type = 0
  UnderTolerance = 0
  UseActualArea = true
  X = 43.5993
  Y = -8.75
FEATURE [TechDraw::DrawViewDimension] Dimension015
  AngleOverride = false
  Arbitrary = false
  ArbitraryTolerances = false
  BoxCorners = (2) [(-35.5,-19,-1e-07),(35.5,19,1e-07)]
  EqualTolerance = true
  ExtensionAngle = 0
  FormatSpec = %.2w
  FormatSpecOverTolerance = %+.2w
  FormatSpecUnderTolerance = %+.2w
  Inverted = false
  LineAngle = 0
  LockPosition = false
  MeasureType = 1
  OverTolerance = 0
  References2D = -> [SectionView]
  Rotation = 0
  ScaleType = 0
  ShowUnits = false
  TheoreticalExact = false
  Type = 0
  UnderTolerance = 0
  UseActualArea = true
  X = 54.3044
  Y = 0
FEATURE [TechDraw::DrawViewDimension] Dimension016
  AngleOverride = false
  Arbitrary = false
  ArbitraryTolerances = false
  BoxCorners = (2) [(-35.5,-19,-1e-07),(35.5,19,1e-07)]
  EqualTolerance = true
  ExtensionAngle = 0
  FormatSpec = %.2w
  FormatSpecOverTolerance = %+.2w
  FormatSpecUnderTolerance = %+.2w
  Inverted = false
  LineAngle = 0
  LockPosition = false
  MeasureType = 1
  OverTolerance = 0
  References2D = -> [SectionView]
  Rotation = 0
  ScaleType = 0
  ShowUnits = false
  TheoreticalExact = false
  Type = 0
  UnderTolerance = 0
  UseActualArea = true
  X = 0
  Y = 10.5532
FEATURE [TechDraw::DrawViewDimension] Dimension017
  AngleOverride = false
  Arbitrary = false
  ArbitraryTolerances = false
  BoxCorners = (2) [(-35.5,-19,-1e-07),(35.5,19,1e-07)]
  EqualTolerance = true
  ExtensionAngle = 0
  FormatSpec = R%.2w
  FormatSpecOverTolerance = %+.2w
  FormatSpecUnderTolerance = %+.2w
  Inverted = false
  LineAngle = 0
  LockPosition = false
  MeasureType = 1
  OverTolerance = 0
  References2D = -> [SectionView]
  Rotation = 0
  ScaleType = 0
  ShowUnits = false
  TheoreticalExact = false
  Type = 4
  UnderTolerance = 0
  UseActualArea = true
  X = 1.01544
  Y = -11.3502
FEATURE [TechDraw::DrawViewDimension] Dimension018
  AngleOverride = false
  Arbitrary = false
  ArbitraryTolerances = false
  BoxCorners = (2) [(-35.5,-19,-1e-07),(35.5,19,1e-07)]
  EqualTolerance = true
  ExtensionAngle = 0
  FormatSpec = %.2w
  FormatSpecOverTolerance = %+.2w
  FormatSpecUnderTolerance = %+.2w
  Inverted = false
  LineAngle = 0
  LockPosition = false
  MeasureType = 1
  OverTolerance = 0
  References2D = -> [SectionView]
  Rotation = 0
  ScaleType = 0
  ShowUnits = false
  TheoreticalExact = false
  Type = 0
  UnderTolerance = 0
  UseActualArea = true
  X = -25.5
  Y = -35.0239
FEATURE [TechDraw::DrawViewDimension] Dimension020
  AngleOverride = false
  Arbitrary = false
  ArbitraryTolerances = false
  BoxCorners = (2) [(-35.5,-35.5,0),(35.5,35.5,0)]
  EqualTolerance = true
  ExtensionAngle = 0
  FormatSpec = ⌀%.2w
  FormatSpecOverTolerance = %+.2w
  FormatSpecUnderTolerance = %+.2w
  Inverted = false
  LineAngle = 0
  LockPosition = false
  MeasureType = 1
  OverTolerance = 0
  References2D = -> [View]
  Rotation = 0
  ScaleType = 0
  ShowUnits = false
  TheoreticalExact = false
  Type = 5
  UnderTolerance = 0
  UseActualArea = true
  X = 44.4591
  Y = -9.76892
FEATURE [TechDraw::DrawViewDimension] Dimension022
  AngleOverride = false
  Arbitrary = false
  ArbitraryTolerances = false
  BoxCorners = (2) [(-35.5,-35.5,0),(35.5,35.5,0)]
  EqualTolerance = true
  ExtensionAngle = 0
  FormatSpec = %.2w
  FormatSpecOverTolerance = %+.2w
  FormatSpecUnderTolerance = %+.2w
  Inverted = false
  LineAngle = 0
  LockPosition = false
  MeasureType = 1
  OverTolerance = 0
  References2D = -> [View]
  Rotation = 0
  ScaleType = 0
  ShowUnits = false
  TheoreticalExact = false
  Type = 2
  UnderTolerance = 0
  UseActualArea = true
  X = -55.3901
  Y = 1e-06
FEATURE [TechDraw::DrawViewDimension] Dimension024
  AngleOverride = false
  Arbitrary = false
  ArbitraryTolerances = false
  BoxCorners = (2) [(-35.5,-35.5,0),(35.5,35.5,0)]
  EqualTolerance = true
  ExtensionAngle = 0
  FormatSpec = %.2w
  FormatSpecOverTolerance = %+.2w
  FormatSpecUnderTolerance = %+.2w
  Inverted = false
  LineAngle = 0
  LockPosition = false
  MeasureType = 1
  OverTolerance = 0
  References2D = -> [View]
  Rotation = 0
  ScaleType = 0
  ShowUnits = false
  TheoreticalExact = false
  Type = 2
  UnderTolerance = 0
  UseActualArea = true
  X = -55.3901
  Y = 1e-06
FEATURE [TechDraw::DrawViewDimension] Dimension026
  AngleOverride = false
  Arbitrary = false
  ArbitraryTolerances = false
  BoxCorners = (2) [(-35.5,-19,-1e-07),(35.5,19,1e-07)]
  EqualTolerance = true
  ExtensionAngle = 0
  FormatSpec = %.2w
  FormatSpecOverTolerance = %+.2w
  FormatSpecUnderTolerance = %+.2w
  Inverted = false
  LineAngle = 0
  LockPosition = false
  MeasureType = 1
  OverTolerance = 0
  References2D = -> [SectionView001]
  Rotation = 0
  ScaleType = 0
  ShowUnits = false
  TheoreticalExact = false
  Type = 1
  UnderTolerance = 0
  UseActualArea = true
  X = 1e-06
  Y = 30.473
FEATURE [TechDraw::DrawViewDimension] Dimension028
  AngleOverride = false
  Arbitrary = false
  ArbitraryTolerances = false
  BoxCorners = (2) [(-35.5,-19,-1e-07),(35.5,19,1e-07)]
  EqualTolerance = true
  ExtensionAngle = 0
  FormatSpec = R%.2w
  FormatSpecOverTolerance = %+.2w
  FormatSpecUnderTolerance = %+.2w
  Inverted = false
  LineAngle = 0
  LockPosition = false
  MeasureType = 1
  OverTolerance = 0
  References2D = -> [SectionView001]
  Rotation = 0
  ScaleType = 0
  ShowUnits = false
  TheoreticalExact = false
  Type = 4
  UnderTolerance = 0
  UseActualArea = true
  X = 1.81787
  Y = -7.63504
FEATURE [TechDraw::DrawViewDimension] Dimension029
  AngleOverride = false
  Arbitrary = false
  ArbitraryTolerances = false
  BoxCorners = (2) [(-35.5,-19,-1e-07),(35.5,19,1e-07)]
  EqualTolerance = true
  ExtensionAngle = 0
  FormatSpec = %.2w
  FormatSpecOverTolerance = %+.2w
  FormatSpecUnderTolerance = %+.2w
  Inverted = false
  LineAngle = 0
  LockPosition = false
  MeasureType = 1
  OverTolerance = 0
  References2D = -> [SectionView]
  Rotation = 0
  ScaleType = 0
  ShowUnits = false
  TheoreticalExact = false
  Type = 0
  UnderTolerance = 0
  UseActualArea = true
  X = -12.0879
  Y = -22.6903
FEATURE [TechDraw::DrawViewDimension] Dimension031
  AngleOverride = false
  Arbitrary = false
  ArbitraryTolerances = false
  BoxCorners = (2) [(-35.5,-19,-1e-07),(35.5,19,1e-07)]
  EqualTolerance = true
  ExtensionAngle = 0
  FormatSpec = %.2w
  FormatSpecOverTolerance = %+.2w
  FormatSpecUnderTolerance = %+.2w
  Inverted = false
  LineAngle = 0
  LockPosition = false
  MeasureType = 1
  OverTolerance = 0
  References2D = -> [SectionView001]
  Rotation = 0
  ScaleType = 0
  ShowUnits = false
  TheoreticalExact = false
  Type = 2
  UnderTolerance = 0
  UseActualArea = true
  X = -47.0135
  Y = -6.76777
FEATURE [TechDraw::DrawViewDimension] Dimension034
  AngleOverride = false
  Arbitrary = false
  ArbitraryTolerances = false
  BoxCorners = (2) [(-35.5,-19,-1e-07),(35.5,19,1e-07)]
  EqualTolerance = true
  ExtensionAngle = 0
  FormatSpec = %.2w
  FormatSpecOverTolerance = %+.2w
  FormatSpecUnderTolerance = %+.2w
  Inverted = false
  LineAngle = 0
  LockPosition = false
  MeasureType = 1
  OverTolerance = 0
  References2D = -> [SectionView001]
  Rotation = 0
  ScaleType = 0
  ShowUnits = false
  TheoreticalExact = false
  Type = 0
  UnderTolerance = 0
  UseActualArea = true
  X = 51.4103
  Y = -25.4165
FEATURE [TechDraw::DrawViewDimension] Dimension035
  AngleOverride = false
  Arbitrary = false
  ArbitraryTolerances = false
  BoxCorners = (2) [(-35.5,-19,-1e-07),(35.5,19,1e-07)]
  EqualTolerance = true
  ExtensionAngle = 0
  FormatSpec = %.2w
  FormatSpecOverTolerance = %+.2w
  FormatSpecUnderTolerance = %+.2w
  Inverted = false
  LineAngle = 0
  LockPosition = false
  MeasureType = 1
  OverTolerance = 0
  References2D = -> [SectionView001]
  Rotation = 0
  ScaleType = 0
  ShowUnits = false
  TheoreticalExact = false
  Type = 0
  UnderTolerance = 0
  UseActualArea = true
  X = 3.50361
  Y = 10.25
FEATURE [TechDraw::DrawViewDimension] Dimension036
  AngleOverride = false
  Arbitrary = false
  ArbitraryTolerances = false
  BoxCorners = (2) [(-35.5,-35.5,0),(35.5,35.5,0)]
  EqualTolerance = true
  ExtensionAngle = 0
  FormatSpec = %.2w
  FormatSpecOverTolerance = %+.2w
  FormatSpecUnderTolerance = %+.2w
  Inverted = false
  LineAngle = 0
  LockPosition = false
  MeasureType = 1
  OverTolerance = 0
  References2D = -> [View]
  Rotation = 0
  ScaleType = 0
  ShowUnits = false
  TheoreticalExact = false
  Type = 6
  UnderTolerance = 0
  UseActualArea = true
  X = 59.5349
  Y = -14.9079
FEATURE [TechDraw::DrawViewDimension] Dimension037
  AngleOverride = false
  Arbitrary = false
  ArbitraryTolerances = false
  BoxCorners = (2) [(-35.5,-19.5,-1e-07),(35.5,19.5,1e-07)]
  EqualTolerance = true
  ExtensionAngle = 0
  FormatSpec = %.2w
  FormatSpecOverTolerance = %+.2w
  FormatSpecUnderTolerance = %+.2w
  Inverted = false
  LineAngle = 0
  LockPosition = false
  MeasureType = 1
  OverTolerance = 0
  References2D = -> [SectionView001]
  Rotation = 0
  ScaleType = 0
  ShowUnits = false
  TheoreticalExact = false
  Type = 0
  UnderTolerance = 0
  UseActualArea = true
  X = -33.7897
  Y = 25.8512
FEATURE [TechDraw::DrawViewDimension] Dimension038
  AngleOverride = false
  Arbitrary = false
  ArbitraryTolerances = false
  BoxCorners = (2) [(-35.5,-19.5,-1e-07),(35.5,19.5,1e-07)]
  EqualTolerance = true
  ExtensionAngle = 0
  FormatSpec = %.2w
  FormatSpecOverTolerance = %+.2w
  FormatSpecUnderTolerance = %+.2w
  Inverted = false
  LineAngle = 0
  LockPosition = false
  MeasureType = 1
  OverTolerance = 0
  References2D = -> [SectionView001]
  Rotation = 0
  ScaleType = 0
  ShowUnits = false
  TheoreticalExact = false
  Type = 0
  UnderTolerance = 0
  UseActualArea = true
  X = -36.6193
  Y = 4.65388
FEATURE [TechDraw::DrawViewDimension] Dimension039
  AngleOverride = false
  Arbitrary = false
  ArbitraryTolerances = false
  BoxCorners = (2) [(-35.5,-19.5,-1e-07),(35.5,19.5,1e-07)]
  EqualTolerance = true
  ExtensionAngle = 0
  FormatSpec = %.2w
  FormatSpecOverTolerance = %+.2w
  FormatSpecUnderTolerance = %+.2w
  Inverted = false
  LineAngle = 0
  LockPosition = false
  MeasureType = 1
  OverTolerance = 0
  References2D = -> [SectionView001]
  Rotation = 0
  ScaleType = 0
  ShowUnits = false
  TheoreticalExact = false
  Type = 0
  UnderTolerance = 0
  UseActualArea = true
  X = -54.0135
  Y = -23.2595
FEATURE [TechDraw::DrawViewDimension] Dimension040
  AngleOverride = false
  Arbitrary = false
  ArbitraryTolerances = false
  BoxCorners = (2) [(-35.5,-19.5,-1e-07),(35.5,19.5,1e-07)]
  EqualTolerance = true
  ExtensionAngle = 0
  FormatSpec = %.2w
  FormatSpecOverTolerance = %+.2w
  FormatSpecUnderTolerance = %+.2w
  Inverted = false
  LineAngle = 0
  LockPosition = false
  MeasureType = 1
  OverTolerance = 0
  References2D = -> [SectionView001]
  Rotation = 0
  ScaleType = 0
  ShowUnits = false
  TheoreticalExact = false
  Type = 6
  UnderTolerance = 0
  UseActualArea = true
  X = 1.04937
  Y = -23.5245
FEATURE [TechDraw::DrawViewDimension] Dimension041
  AngleOverride = false
  Arbitrary = false
  ArbitraryTolerances = false
  BoxCorners = (2) [(-35.5,-19.5,-1e-07),(35.5,19.5,1e-07)]
  EqualTolerance = true
  ExtensionAngle = 0
  FormatSpec = %.2w
  FormatSpecOverTolerance = %+.2w
  FormatSpecUnderTolerance = %+.2w
  Inverted = false
  LineAngle = 0
  LockPosition = false
  MeasureType = 1
  OverTolerance = 0
  References2D = -> [SectionView001]
  Rotation = 0
  ScaleType = 0
  ShowUnits = false
  TheoreticalExact = false
  Type = 0
  UnderTolerance = 0
  UseActualArea = true
  X = -3.49639
  Y = 10.25
FEATURE [TechDraw::DrawViewDimension] Dimension042
  AngleOverride = false
  Arbitrary = false
  ArbitraryTolerances = false
  BoxCorners = (2) [(-35.5,-19.5,-1e-07),(35.5,19.5,1e-07)]
  EqualTolerance = true
  ExtensionAngle = 0
  FormatSpec = %.2w
  FormatSpecOverTolerance = %+.2w
  FormatSpecUnderTolerance = %+.2w
  Inverted = false
  LineAngle = 0
  LockPosition = false
  MeasureType = 1
  OverTolerance = 0
  References2D = -> [SectionView001]
  Rotation = 0
  ScaleType = 0
  ShowUnits = false
  TheoreticalExact = false
  Type = 1
  UnderTolerance = 0
  UseActualArea = true
  X = -17.5
  Y = 30.473
FEATURE [TechDraw::DrawViewAnnotation] Annotation
  Font = osifont
  LineSpace = 100
  LockPosition = false
  MaxWidth = -1
  Rotation = 0
  ScaleType = 0
  Text = 2022/241806
  TextSize = 5
  TextStyle = 0
  X = 213.04
  Y = 34.112
FEATURE [TechDraw::DrawViewDimension] Dimension043
  AngleOverride = false
  Arbitrary = false
  ArbitraryTolerances = false
  BoxCorners = (2) [(-35.5,-35.5,0),(35.5,35.5,0)]
  EqualTolerance = true
  ExtensionAngle = 0
  FormatSpec = ⌀%.2w
  FormatSpecOverTolerance = %+.2w
  FormatSpecUnderTolerance = %+.2w
  Inverted = false
  LineAngle = 0
  LockPosition = false
  MeasureType = 1
  OverTolerance = 0
  References2D = -> [View]
  Rotation = 0
  ScaleType = 0
  ShowUnits = false
  TheoreticalExact = false
  Type = 5
  UnderTolerance = 0
  UseActualArea = true
  X = 24.0778
  Y = -31.2589
FEATURE [TechDraw::DrawProjGroupItem] View002
  CoarseView = false
  Direction = (-0.57735,-0.57735,0.57735)
  Focus = 100
  HardHidden = false
  IsoCount = 0
  IsoHidden = false
  IsoVisible = false
  LockPosition = false
  Perspective = false
  Rotation = 0
  RotationVector = (1,0,0)
  ScaleType = 0
  ScrubCount = 1
  SeamHidden = false
  SeamVisible = false
  SmoothHidden = false
  SmoothVisible = true
  Source = -> [Body]
  Type = 0
  X = 204.33
  XDirection = (0.707107,-0.707107,0)
  Y = 161.598
FEATURE [TechDraw::DrawPage] Page
  KeepUpdated = true
  NextBalloonIndex = 1
  ProjectionType = 0
  Template = -> Template
  Views = -> [View,SectionView,View001,SectionView001,Dimension,Dimension002,Dimension003,Dimension004,Dimension006,Dimension007,Dimension008,Dimension009,Dimension010,Dimension011,Dimension013,Dimension014,Dimension015,Dimension016,Dimension017,Dimension018,Dimension020,Dimension022,Dimension024,Dimension026,Dimension028,Dimension029,Dimension031,Dimension034,Dimension035,Dimension036,Dimension037,+8 more]
